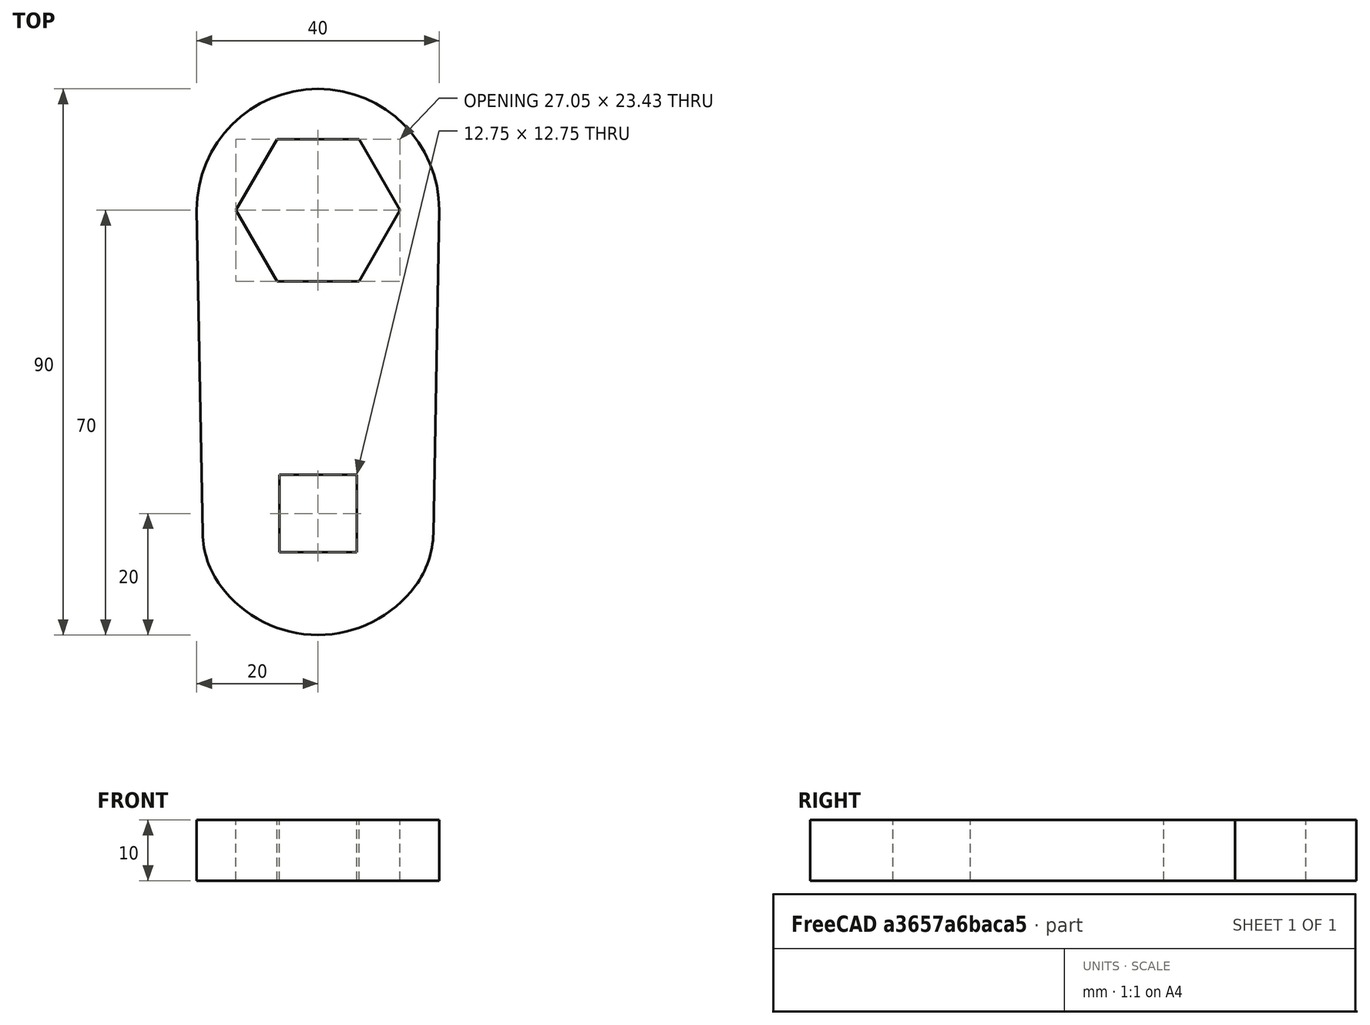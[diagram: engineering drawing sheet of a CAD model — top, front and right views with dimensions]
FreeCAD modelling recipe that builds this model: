
FCSTD DOCUMENT  (FreeCAD 0.18R16131 (Git))
Label: transmission wrench 27 13 w fea
License: All rights reserved
LicenseURL: http://en.wikipedia.org/wiki/All_rights_reserved
objects: Fem::FemMeshObjectPython×2, Sketcher::SketchObject×1, PartDesign::Pad×1, PartDesign::Fillet×1, PartDesign::Body×1, Fem::FemSolverObjectPython×1, Fem::ConstraintFixed×1, Fem::ConstraintForce×1, App::MaterialObjectPython×1, Fem::FemResultObjectPython×1, Fem::FemAnalysis×1
note: 5 computed .brp shape members not serialized (recipe doc carries the construction recipe); baked Part::Feature solids carry a one-line shape summary decoded from their .brp

FEATURE [Sketcher::SketchObject] Sketch
  MapMode = 5
  Support = -> [XY_Plane]
  expr: Constraints[29] = 25.4 * 0.5 + 0.05
  sketch-geometry (17):
    g0: LineSegment StartX=-13.525 StartY=0 StartZ=0 EndX=-6.7625 EndY=-11.713 EndZ=0
    g1: LineSegment StartX=-6.7625 StartY=-11.713 StartZ=0 EndX=6.7625 EndY=-11.713 EndZ=0
    g2: LineSegment StartX=6.7625 StartY=-11.713 StartZ=0 EndX=13.525 EndY=0 EndZ=0
    g3: LineSegment StartX=13.525 StartY=0 StartZ=0 EndX=6.7625 EndY=11.713 EndZ=0
    g4: LineSegment StartX=6.7625 StartY=11.713 StartZ=0 EndX=-6.7625 EndY=11.713 EndZ=0
    g5: LineSegment StartX=-6.7625 StartY=11.713 StartZ=0 EndX=-13.525 EndY=0 EndZ=0
    g6: Circle [constr] CenterX=0 CenterY=0 CenterZ=0 NormalX=0 NormalY=0 NormalZ=1 AngleXU=0 Radius=13.525
    g7: LineSegment StartX=6.375 StartY=-56.375 StartZ=0 EndX=6.375 EndY=-43.625 EndZ=0
    g8: LineSegment StartX=6.375 StartY=-43.625 StartZ=0 EndX=-6.375 EndY=-43.625 EndZ=0
    g9: LineSegment StartX=-6.375 StartY=-43.625 StartZ=0 EndX=-6.375 EndY=-56.375 EndZ=0
    g10: LineSegment StartX=-6.375 StartY=-56.375 StartZ=0 EndX=6.375 EndY=-56.375 EndZ=0
    g11: Circle [constr] CenterX=0 CenterY=-50 CenterZ=0 NormalX=0 NormalY=0 NormalZ=1 AngleXU=0 Radius=9.01561
    g12: ArcOfCircle CenterX=0 CenterY=0 CenterZ=0 NormalX=0 NormalY=0 NormalZ=1 AngleXU=0 Radius=20 StartAngle=4.8e-15 EndAngle=3.14159
    g13: ArcOfCircle CenterX=0 CenterY=-50 CenterZ=0 NormalX=0 NormalY=0 NormalZ=1 AngleXU=0 Radius=20 StartAngle=3.466 EndAngle=5.95877
    g14: LineSegment StartX=-20 StartY=0 StartZ=0 EndX=-18.9568 EndY=-56.375 EndZ=0
    g15: LineSegment StartX=18.9568 StartY=-56.375 StartZ=0 EndX=20 EndY=0 EndZ=0
    g16: LineSegment [constr] StartX=-18.9568 StartY=-56.375 StartZ=0 EndX=18.9568 EndY=-56.375 EndZ=0
  constraints (44):
    c: Coincident(g0,g1)
    c: Coincident(g1,g2)
    c: Coincident(g2,g3)
    c: Coincident(g3,g4)
    c: Coincident(g4,g5)
    c: Coincident(g5,g0)
    c: Equal(g0, g1-g5) x5
    c: PointOnObject(g0,g6)
    c: PointOnObject(g1,g6)
    c: PointOnObject(g2,g6)
    c: PointOnObject(g3,g6)
    c: Symmetric(g0,g2,g-1)
    c: Coincident(g7,g8)
    c: Coincident(g8,g9)
    c: Coincident(g9,g10)
    c: Coincident(g10,g7)
    c: Equal(g7,g8)
    c: Equal(g7,g9)
    c: Equal(g7,g10)
    c: PointOnObject(g7,g11)
    c: PointOnObject(g8,g11)
    c: PointOnObject(g9,g11)
    c: PointOnObject(g10,g11)
    c: PointOnObject(g11,g-2)
    c: Parallel(g8,g-1)
    c: DistanceX(g9,g7) = 12.75
    c: DistanceY(g11,g-1) = 50
    c: PointOnObject(g12,g-1)
    c: PointOnObject(g12,g-1)
    c: Coincident(g14,g12)
    c: Coincident(g15,g12)
    c: Coincident(g12,g-1)
    c: Radius(g12) = 20
    c: Radius(g13) = 20
    c: Coincident(g15,g13)
    c: Coincident(g13,g14)
    c: Coincident(g13,g11)
    c: Coincident(g13,g16)
    c: Coincident(g16,g13)
    c: Parallel(g16,g-1)
    c: PointOnObject(g7,g16)
    c: Coincident(g6,g12)
    c: PointOnObject(g0,g-1)
    c: DistanceX(g0,g2) = 27.05
FEATURE [PartDesign::Pad] Pad
  Length = 10
  Length2 = 100
  Profile = -> Sketch
  Type = 0
FEATURE [PartDesign::Fillet] Fillet
  Base = -> Pad [Edge2,Edge5,Edge8,Edge1]
  BaseFeature = -> Pad
  Radius = 15
FEATURE [PartDesign::Body] Body
  Group = -> [Sketch,Pad,Fillet]
  Origin = -> Origin
  Tip = -> Fillet
FEATURE [Fem::FemSolverObjectPython] CalculiXccxTools  # FEM object (typed FeaturePython)
  AnalysisType = 0
  BeamShellResultOutput3D = false
  EigenmodeHighLimit = 1000000
  EigenmodeLowLimit = 0
  EigenmodesCount = 10
  GeometricalNonlinearity = 0
  IterationsControlParameterCutb = 0.25,0.5,0.75,0.85,,,1.5,
  IterationsControlParameterIter = 4,8,9,200,10,400,,200,,
  IterationsControlParameterTimeUse = false
  IterationsThermoMechMaximum = 200
  IterationsUserDefinedIncrementations = false
  IterationsUserDefinedTimeStepLength = false
  MaterialNonlinearity = 0
  MatrixSolverType = 0
  SplitInputWriter = false
  ThermoMechSteadyState = true
  TimeEnd = 1
  TimeInitialStep = 1
FEATURE [Fem::FemMeshObjectPython] FEMMeshGmsh  # FEM object (typed FeaturePython)
  Algorithm2D = 0
  Algorithm3D = 0
  CharacteristicLengthMax = 0
  CharacteristicLengthMin = 0
  CoherenceMesh = true
  ElementDimension = 0
  ElementOrder = 1
  GeometryTolerance = 1e-06
  GroupsOfNodes = false
  HighOrderOptimize = false
  OptimizeNetgen = false
  OptimizeStd = true
  Part = -> Fillet
  RecombineAll = false
FEATURE [Fem::ConstraintFixed] FemConstraintFixed
  NormalDirection = (0.866025,-0.5,0)
  Normals = (54) [(0.866025,-0.5,0),(0.866025,-0.5,0),(0.866025,-0.5,0),(0.866025,-0.5,0),(0.866025,-0.5,0),(0.866025,-0.5,0),(0.866025,-0.5,0),(0.866025,-0.5,0),+46 more]
  Points = (54) [(-6.7625,11.713,10),(-10.1438,5.8565,10),(-13.525,0,10),(-6.7625,11.713,5),(-10.1438,5.8565,5),(-13.525,0,5),(-6.7625,11.713,0),(-10.1438,5.8565,0),+46 more]
  References = -> [Fillet]
FEATURE [Fem::ConstraintForce] FemConstraintForce
  DirectionVector = (-1,0,0)
  Force = 8300
  NormalDirection = (1,0,0)
  Points = (9) [(-6.375,-43.625,10),(-6.375,-50,10),(-6.375,-56.375,10),(-6.375,-43.625,5),(-6.375,-50,5),(-6.375,-56.375,5),(-6.375,-43.625,0),(-6.375,-50,0),+1 more]
  References = -> [Fillet]
  Reversed = true
FEATURE [App::MaterialObjectPython] SolidMaterial  # material (typed FeaturePython)
  Category = 0
  Material = Density=7900 kg/m^3,Description=Standard steel material for CalculiX sample calculations,Father=Metal,Name=CalculiX-Steel,PoissonRatio=0.3,+4 more (map truncated)
FEATURE [Fem::FemMeshObjectPython] Result_mesh  # FEM object (typed FeaturePython)
FEATURE [Fem::FemResultObjectPython] CalculiX_static_results  # FEM object (typed FeaturePython)
  DisplacementLengths = [0.0525774,0.0024483,0.0525848,0.00244872,0.0590407,0.00243676,0.0574008,0.0478227,0,0,0,0,0,0,0.0533955,0.0497447,0.0329751,0.0298357,0.0590454,0.00243436,0.057423,0.0478387,0,0,0,0,0,0,0.0534019,0.0497632,0.0329787,0.0298432,0.00572885,+1396 more]
  DisplacementVectors = (1429) [(-0.0492539,0.0183941,0.000305558),(-0.000239162,0.00241331,-0.000335987),(-0.0492634,0.0183887,-0.000368564),(-0.000231604,0.00241354,0.000342629),+1425 more]
  Eigenmode = 0
  EigenmodeFrequency = 0
  MaxShear = [25.3612,21.4058,26.9441,21.4275,19.4342,21.8417,10.7652,2.29886,5.97426,34.93,5.82914,33.8923,63.4113,58.3395,30.9532,35.8435,72.604,34.5402,19.2569,21.5168,10.6713,2.46788,5.98002,34.802,5.8896,34.6482,60.2646,60.7773,30.4765,35.9353,+1399 more]
  Mesh = -> Result_mesh
  NodeNumbers = [1,2,3,4,5,6,7,8,9,10,11,12,13,14,15,16,17,18,19,20,21,22,23,24,25,26,27,28,29,30,31,32,33,34,35,36,37,38,39,40,41,42,43,44,45,46,47,48,49,50,51,52,53,54,55,56,57,58,59,60,61,62,63,64,65,66,67,68,69,+1360 more]
  PrincipalMax = [50.4649,3.10255,53.4186,2.89007,38.4293,41.642,0.215424,3.60735,5.5234,23.0038,7.01908,45.6756,96.6051,31.1315,2.40339,75.9023,152.62,-5.94506,37.8708,41.6384,0.458008,4.26998,5.54689,23.0587,7.24069,48.1167,88.2934,30.936,2.25122,76.2105,+1399 more]
  PrincipalMed = [0.0355426,-0.876329,0.561895,-1.01252,0.732135,0.267654,0.0752514,-0.256468,-0.0733678,-5.39893,0.547849,4.02819,19.3412,-15.4291,-7.28786,19.4918,15.2104,-19.0269,0.582337,-0.0416599,0.104913,-0.34787,-0.0602111,-5.13303,0.62363,4.6935,+1403 more]
  PrincipalMin = [-0.257391,-39.709,-0.469592,-39.9649,-0.439098,-2.04128,-21.315,-0.990372,-6.42512,-46.8562,-4.63919,-22.1089,-30.2175,-85.5476,-59.503,4.21532,7.41231,-75.0254,-0.643132,-1.39512,-20.8845,-0.665781,-6.41316,-46.5453,-4.53851,-21.1797,+1403 more]
  ResultType = Fem::FemResultMechanical
  Stats = [-0.0625385,-0.022636,0.000356029,-0.0186118,0.000280296,0.0196531,-0.00104853,-1.07731e-05,0.001012,0,0.0238873,0.0625386,0.181671,49.0626,167.523,-18.808,28.1495,201.217,-79.2272,-0.851807,40.1346,-119.604,-25.2335,27.921,0.103378,26.6915,+13 more]
  StrainVectors = (1429) [(-7.13427e-05,0.000238469,-7.14249e-05),(4.71371e-05,-0.000190584,7.20516e-05),(-7.63186e-05,0.000252264,-7.40198e-05),+1426 more]
  StressValues = [50.5765,40.9672,53.38,41.0431,38.2963,42.5758,21.4607,4.27825,10.3546,60.8517,10.1168,59.2131,110.702,101.731,57.6747,65.4008,141.47,63.5574,37.916,42.373,21.1682,4.78474,10.3644,60.6402,10.227,60.6506,105.089,106.009,56.7648,65.5383,+1399 more]
  StressVectors = (1429) [(0.0699721,50.1164,0.0566925),(-1.03539,-39.4366,2.98924),(0.0202951,53.099,0.391639),(-1.20848,-39.7331,2.85421),(14.14,23.8527,0.729683),+1424 more]
  Time = 0
FEATURE [Fem::FemAnalysis] Analysis
  Group = -> [CalculiXccxTools,FEMMeshGmsh,FemConstraintFixed,FemConstraintForce,SolidMaterial,CalculiX_static_results]
